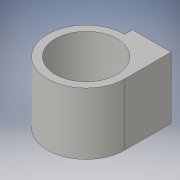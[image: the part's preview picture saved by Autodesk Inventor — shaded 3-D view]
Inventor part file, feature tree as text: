
AUTODESK INVENTOR PART (.ipt)
format: ipt  version: 2016 (Build 200138000, 138)  size: 116,736 bytes
history: native  units: in
note: dims shown in document units (in); Inventor stores cm internally (conversion verified against a paired STEP export)
features: extrude x3, sketch x3
ambient origin geometry x8: Origin, YZ Plane, XZ Plane, XY Plane, X Axis, Y Axis, Z Axis, Center Point
bodies: Solid1 (feature_tree)
feature tree (6):
  extrude  "Extrusion1"  Depth=1.25in
  extrude  "Extrusion2"  Depth=0.25in TaperAngle=0.0deg
  extrude  "Extrusion3"  Depth=0.25in
  sketch  "Sketch1"  dims[d0=1.0in d1=1.25in]
  sketch  "Sketch2"  dims[d2=0.25in d3=1.0in d4=0.0in]
  sketch  "Sketch3"  dims[d5=0.2in d6=0.3125in d7=0.515in d8=0.0in d9=0.25in d10=0.3125in d11=0.25in d12=0.0in]
